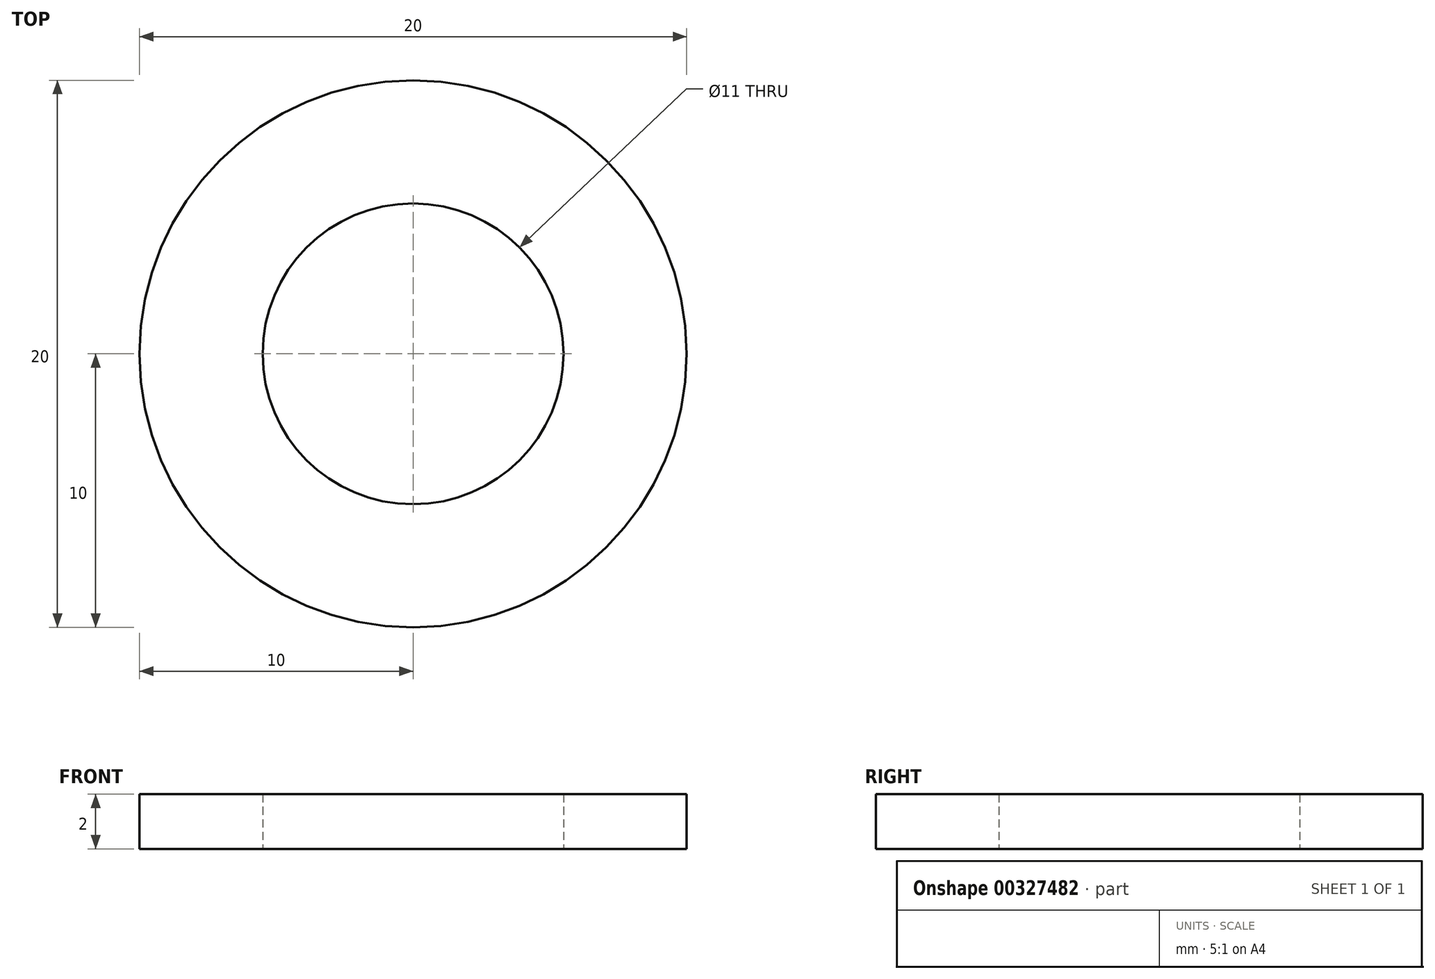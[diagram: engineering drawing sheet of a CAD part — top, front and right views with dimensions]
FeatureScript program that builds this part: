
annotation { "Feature Type Name" : "Feature", "Feature Type Description" : "" }
export const myFeature = defineFeature(function(context is Context, id is Id, definition is map)
    precondition{}
    {
        {
            var Q0;
            Q0=qCreatedBy(makeId("Top.planeOp"),FACE);
            var sketch = newSketch(context, id + "F0", { "sketchPlane" : qUnion([Q0])});
            skCircle(sketch, "E0", {"center": v(0, 0) * mm, "radius": 10 * mm});
            skCircle(sketch, "E1", {"center": v(0, 0) * mm, "radius": 5.5 * mm});
            skSolve(sketch);
        }
        {
            var Q0;
            Q0 = qSketchRegion(id + "F0", true);
            var Q1;
            Q1=makeQuery(id+"F0.imprint","IMPRINT",FACE,{"disambiguationData":[TD([[makeQuery(id+"F0.imprint","IMPRINT",EDGE,{"derivedFrom":sQuery(id+"F0.wireOp",EDGE,"E0")}),1.0]])]});
            extrude(context, id + "F1", {"entities" : qUnion([Q0, Q1]), "depth" : 2 * mm});
        }
    });
